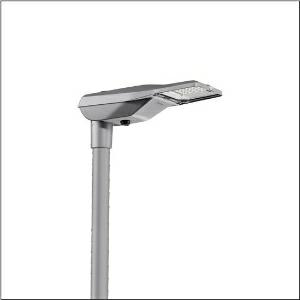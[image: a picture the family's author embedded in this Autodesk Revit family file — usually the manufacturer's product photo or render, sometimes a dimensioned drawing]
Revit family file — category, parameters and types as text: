
# Revit family: streetlight_sl_21_micro___p0_8ab_5xe1r33r08db_894c
name_source: partatom
category: Lighting Fixtures
units: mm (PartAtom-declared; Revit-internal decimal feet)

## family parameters
Cut with Voids When Loaded = No
Host = Face
Light Source = No
Part Type = Normal
Room Calculation Point = No
Round Connector Dimension = Use Diameter
Shared = No

## types (1)
- --- (1 x LED, 4470 lm, 39.1 W, 3000K)
    Apparent Load = 39 VA
    CIE Flux Codes = 36 71 98 100 100
    Color Rendering = 70
    Color Temperature = 3000K
    Default Elevation = 1800 mm
    Description = Streetlight SL 21 micro, mast luminaire, primary light control with lens, of PMMA, primary optical cover: cover, of toughened safety glass, transparent, light distribution: P0.8aB, light emission: direct distribution, primary light characteristic: asymmetric, installation type: post-top, side-entry, LED, High Power LED, rated luminous flux: 4.470lm, luminous efficacy: 114lm/W, light colour: 730, colour temperature: 3000K, control gear: D4i, control: pre-setting: logarithmic dimming characteristic, flexible luminous flux parameterisation, time-dependent luminous flux control, constant luminous flux control, overheat protection, mains connection: 220..240V, AC, 50/60Hz, start of lifetime: 39W, end of service life: 41W, reduction: 18W, luminaire housing, of diecast aluminium, powder-coated, Siteco® metallic grey (DB 702S), corrosivity category C5 mid according to DIN EN ISO 12944, multi-level sealing system, sealing non-destructively replaceable, inclination adjustable: 0°, 5°, 10°, 15°, please order mast flange separately, length: 528mm, width: 235mm, height: 110mm, mast flange for spigot size: 42mm (side-entry): 5XC10008XM4, 60/48mm (side-entry/post-top): 5XC10108XM2, 76/60mm (side-entry/post-top): 5XC10108XM1, Smart Interface below, protection rating (complete): IP66, insulation class (complete): insulation class II (safety insulation), certification: CE, ENEC, ENEC+, VDE, impact resistance: IK10, permissible operating ambient temperature for outdoor applications: -40..+50°C, standard-compliant lighting for roads and squares, packaging unit: 1 piece

Light Distribution: P0.8aB
    Height = 110 mm
    Lamp = 1 x LED
    Lamp Light Flux = 4470 lm
    Lamp Power = 39.1 W
    Lamp count = 1
    Length = 528 mm
    Luminous efficacy = 114 lm/W
    Manufacturer = Siteco
    ModVariant = No
    Model = 5XE1R33R08DB
    Number of Poles = 1
    OnlyDefault = Yes
    Power Factor = 1
    Product Name = Streetlight SL 21 micro | P0.8aB
    Product group = mast luminaire | pylon top
    ProductGroupID = 6100
    Protection Class = Protection class II
    Protection Degree = IP 66
    RLX_Detail_Level = 1
    RLX_Emergency_Light_Flux = 0 lm
    RLX_Emergency_Type = 0
    RLX_Emergency_Type_DB = No
    RlxData = <blob elided: 98409 chars, md5=dbb15c69>
    Socket = socket
    Standby Power = 0 W
    System Light Flux = 4470 lm
    System Power = 39 W
    Type Comments = factory setting: luminous flux: 100 % | dim-lin: 254 | 765 mA
    Type Image = l_1277290.jpg
    URL = http://relux.com
    VarID = @adj_075158
    Voltage = 0 V
    Weight = 0.00 kg
    Width = 235 mm

## geometry (parser evidence)
native form markers: Blend x4, Sweep x11
no freeform markers — native parametric forms only
